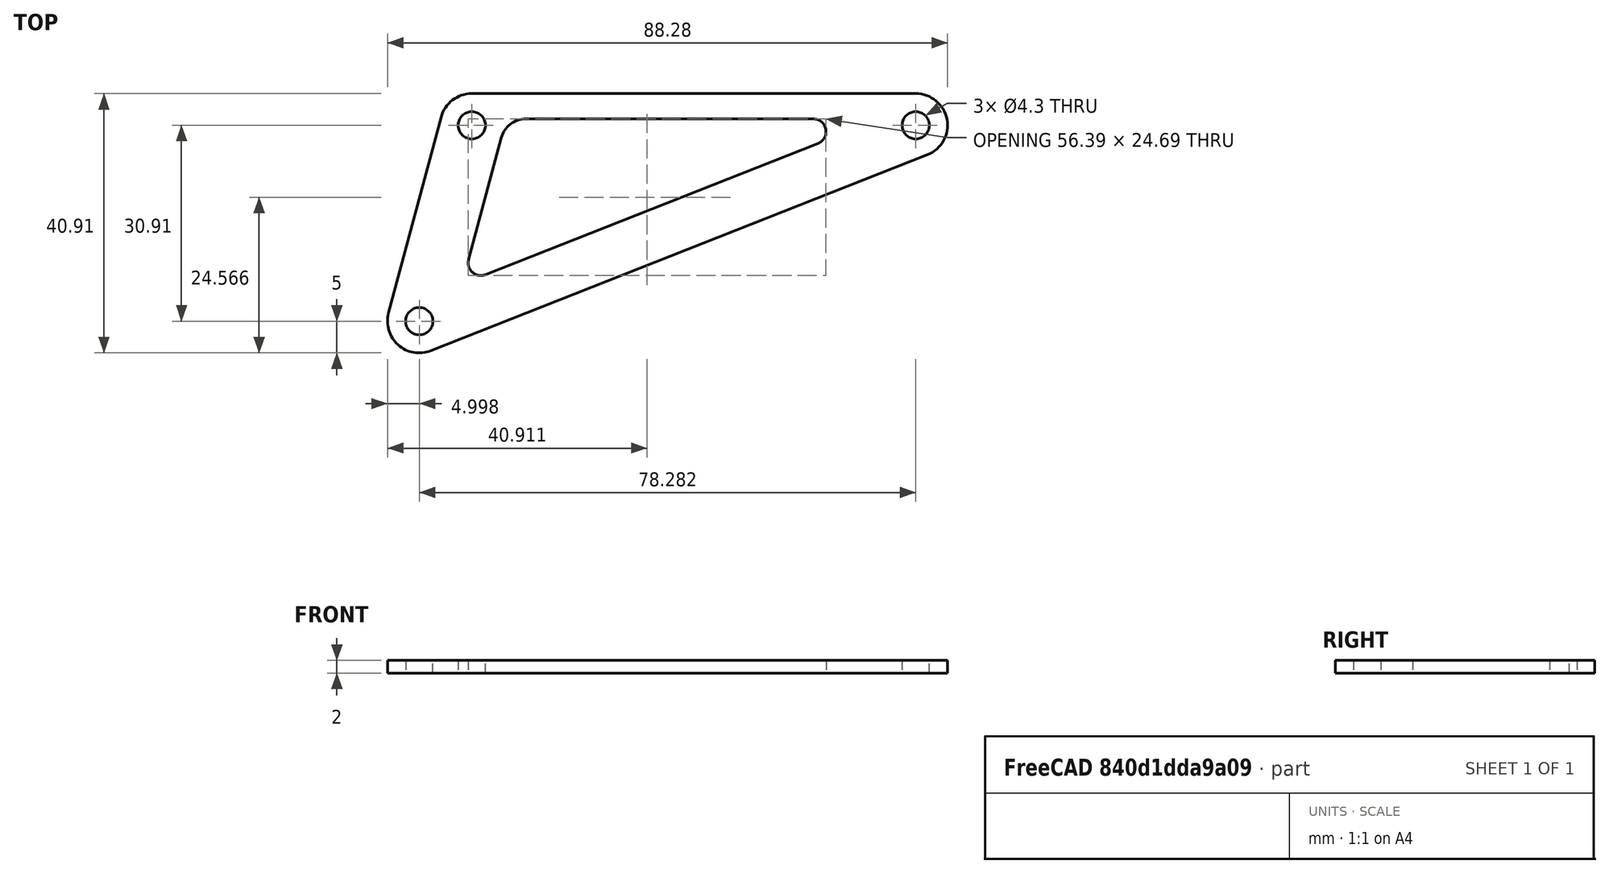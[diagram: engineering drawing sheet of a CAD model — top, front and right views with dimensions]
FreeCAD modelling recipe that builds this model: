
FCSTD DOCUMENT  (FreeCAD 0.20R29177 +426 (Git))
Label: BreakawayHeadTrussShort
License: All rights reserved
LicenseURL: http://en.wikipedia.org/wiki/All_rights_reserved
objects: App::DocumentObjectGroup×3, PartDesign::CoordinateSystem×1, App::FeaturePython×1, Sketcher::SketchObject×1, PartDesign::Pad×1, PartDesign::Body×1, App::Part×1
note: 5 computed .brp shape members not serialized (recipe doc carries the construction recipe); baked Part::Feature solids carry a one-line shape summary decoded from their .brp
EXTERNAL_REF file=BreakawayHeadBase.FCStd obj=Sketch002
EXTERNAL_REF file=Params.FCStd obj=Spreadsheet

FEATURE [App::DocumentObjectGroup] Parts
FEATURE [PartDesign::CoordinateSystem] LCS_Origin
  AttacherType = Attacher::AttachEngine3D
  MapMode = 2
  Support = -> [X_Axis]
FEATURE [App::FeaturePython] Variables  # WARN: FeaturePython — macro-defined, semantics opaque (R4)
  CompressionWidth = 8
  InternalRadius = 2
  TensionWidth = 4
  TrussAngle = 15
  Type = App::PropertyContainer
FEATURE [App::DocumentObjectGroup] Constraints
FEATURE [App::DocumentObjectGroup] Configurations
FEATURE [Sketcher::SketchObject] Sketch
  FullyConstrained = true
  MapMode = 5
  Support = -> [XY_Plane001]
  expr: Constraints[12] = 90 - <<Variables>>.TrussAngle
  expr: Constraints[26] = <<Variables>>.TensionWidth
  expr: Constraints[45] = <<Variables>>.CompressionWidth
  expr: Constraints[55] = <<Params>>#<<Params>>.CablePulleyDiameter
  expr: Constraints[9] = <<BreakawayHeadBase>>#<<Sketch002>>.Constraints.TrussHoleSpacing
  sketch-geometry (24):
    g0: Circle CenterX=0 CenterY=0 CenterZ=0 NormalX=0 NormalY=0 NormalZ=1 AngleXU=0 Radius=2.15
    g1: ArcOfCircle CenterX=0 CenterY=0 CenterZ=0 NormalX=0 NormalY=0 NormalZ=1 AngleXU=0 Radius=5 StartAngle=1.5708 EndAngle=2.87979
    g2: ArcOfCircle CenterX=-8.28221 CenterY=-30.9096 CenterZ=0 NormalX=0 NormalY=0 NormalZ=1 AngleXU=0 Radius=5 StartAngle=2.87979 EndAngle=5.08845
    g3: LineSegment StartX=-13.1118 StartY=-29.6155 StartZ=0 EndX=-4.82963 EndY=1.2941 EndZ=0
    g4: LineSegment StartX=71.8363 StartY=-4.6506 StartZ=0 EndX=-6.44593 EndY=-35.5602 EndZ=0
    g5: LineSegment StartX=0 StartY=0 StartZ=0 EndX=-8.28221 EndY=-30.9096 EndZ=0
    g6: Circle CenterX=-8.28221 CenterY=-30.9096 CenterZ=0 NormalX=0 NormalY=0 NormalZ=1 AngleXU=0 Radius=2.15
    g7: LineSegment StartX=6e-16 StartY=5 StartZ=0 EndX=70 EndY=5 EndZ=0
    g8: ArcOfCircle CenterX=70 CenterY=0 CenterZ=0 NormalX=0 NormalY=0 NormalZ=1 AngleXU=0 Radius=5 StartAngle=5.08845 EndAngle=7.85398
    g9: GeomPoint X=96.2775 Y=5 Z=0
    g10: Circle CenterX=70 CenterY=0 CenterZ=0 NormalX=0 NormalY=0 NormalZ=1 AngleXU=0 Radius=2.15
    g11: LineSegment StartX=2.1675 StartY=-23.5582 StartZ=0 EndX=54.5874 EndY=-2.86024 EndZ=0
    g12: LineSegment StartX=53.8529 StartY=1 StartZ=0 EndX=8.51364 EndY=1 EndZ=0
    g13: LineSegment StartX=4.64993 StartY=-1.96472 StartZ=0 EndX=-0.498864 EndY=-21.1803 EndZ=0
    g14: ArcOfCircle CenterX=53.8529 CenterY=-1 CenterZ=0 NormalX=0 NormalY=0 NormalZ=1 AngleXU=0 Radius=2 StartAngle=5.08845 EndAngle=7.85398
    g15: GeomPoint X=64.3639 Y=1 Z=0
    g16: ArcOfCircle CenterX=1.43299 CenterY=-21.6979 CenterZ=0 NormalX=0 NormalY=0 NormalZ=1 AngleXU=0 Radius=2 StartAngle=2.87979 EndAngle=5.08845
    g17: GeomPoint X=-1.52688 Y=-25.0169 Z=0
    g18: ArcOfCircle CenterX=8.51364 CenterY=-3 CenterZ=0 NormalX=0 NormalY=0 NormalZ=1 AngleXU=0 Radius=4 StartAngle=1.5708 EndAngle=2.87979
    g19: GeomPoint X=5.44433 Y=1 Z=0
    g20: LineSegment StartX=2.1675 StartY=-23.5582 StartZ=0 EndX=5.10555 EndY=-30.9991 EndZ=0
    g21: LineSegment StartX=-0.498864 StartY=-21.1803 StartZ=0 EndX=-5.32849 EndY=-19.8862 EndZ=0
    g22: LineSegment StartX=-5.32849 StartY=-19.8862 StartZ=0 EndX=-10.1581 EndY=-18.5921 EndZ=0
    g23: Circle CenterX=70 CenterY=0 CenterZ=0 NormalX=0 NormalY=0 NormalZ=1 AngleXU=0 Radius=60
  constraints (56):
    c: Diameter(g0) = 4.3
    c: Tangent(g2,g3) = 1.5708
    c: Tangent(g3,g1) = 1.5708
    c: Tangent(g4,g2) = 1.5708
    c: Radius(g1) = 5
    c: Coincident(g1,g0)
    c: Equal(g2,g1)
    c: Coincident(g5,g0)
    c: Coincident(g5,g2)
    c: Distance(g5) = 32
    c: Coincident(g6,g2)
    c: Equal(g6,g0)
    c: Angle(g-1,g5) = 1.309
    c: Coincident(g0,g-1)
    c: Horizontal(g7)
    c: Tangent(g7,g1) = 1.5708
    c: PointOnObject(g9,g7)
    c: PointOnObject(g9,g4)
    c: Tangent(g7,g8) = 1.5708
    c: Tangent(g4,g8) = 1.5708
    c: PointOnObject(g8,g-1)
    c: Coincident(g10,g8)
    c: Equal(g10,g0)
    c: Horizontal(g12)
    c: Parallel(g11,g4)
    c: Parallel(g13,g3)
    c: DistanceY(g15,g7) = 4
    c: PointOnObject(g15,g12)
    c: PointOnObject(g15,g11)
    c: Tangent(g12,g14) = -1.5708
    c: Tangent(g11,g14) = -1.5708
    c: PointOnObject(g17,g11)
    c: PointOnObject(g17,g13)
    c: Tangent(g11,g16) = -1.5708
    c: Tangent(g13,g16) = -1.5708
    c: PointOnObject(g19,g13)
    c: PointOnObject(g19,g12)
    c: Tangent(g13,g18) = -1.5708
    c: Tangent(g12,g18) = -1.5708
    c: Equal(g16,g14)
    c: Radius(g14) = 2
    c: Radius(g18) = 4
    c: Coincident(g20,g11)
    c: PointOnObject(g20,g4)
    c: Perpendicular(g4,g20)
    c: Distance(g20) = 8
    c: Coincident(g21,g13)
    c: PointOnObject(g21,g5)
    c: Coincident(g22,g21)
    c: PointOnObject(g22,g3)
    c: PointOnObject(g22,g21)
    c: Perpendicular(g13,g21)
    c: Equal(g21,g22)
    c: DistanceX(g0,g8) = 70
    c: Coincident(g23,g8)
    c: Diameter(g23) = 120
FEATURE [PartDesign::Pad] Pad
  Direction = (0,0,1)
  Length = 2
  Length2 = 10
  Profile = -> Sketch
  ReferenceAxis = -> Sketch [N_Axis]
  Type = 0
FEATURE [PartDesign::Body] Body
  Group = -> [Sketch,Pad]
  Origin = -> Origin001
  Tip = -> Pad
FEATURE [App::Part] Assembly
  AssemblyType = Part::Link
  Group = -> [LCS_Origin,Variables,Constraints,Configurations,Body]
  Origin = -> Origin
  Type = Assembly
